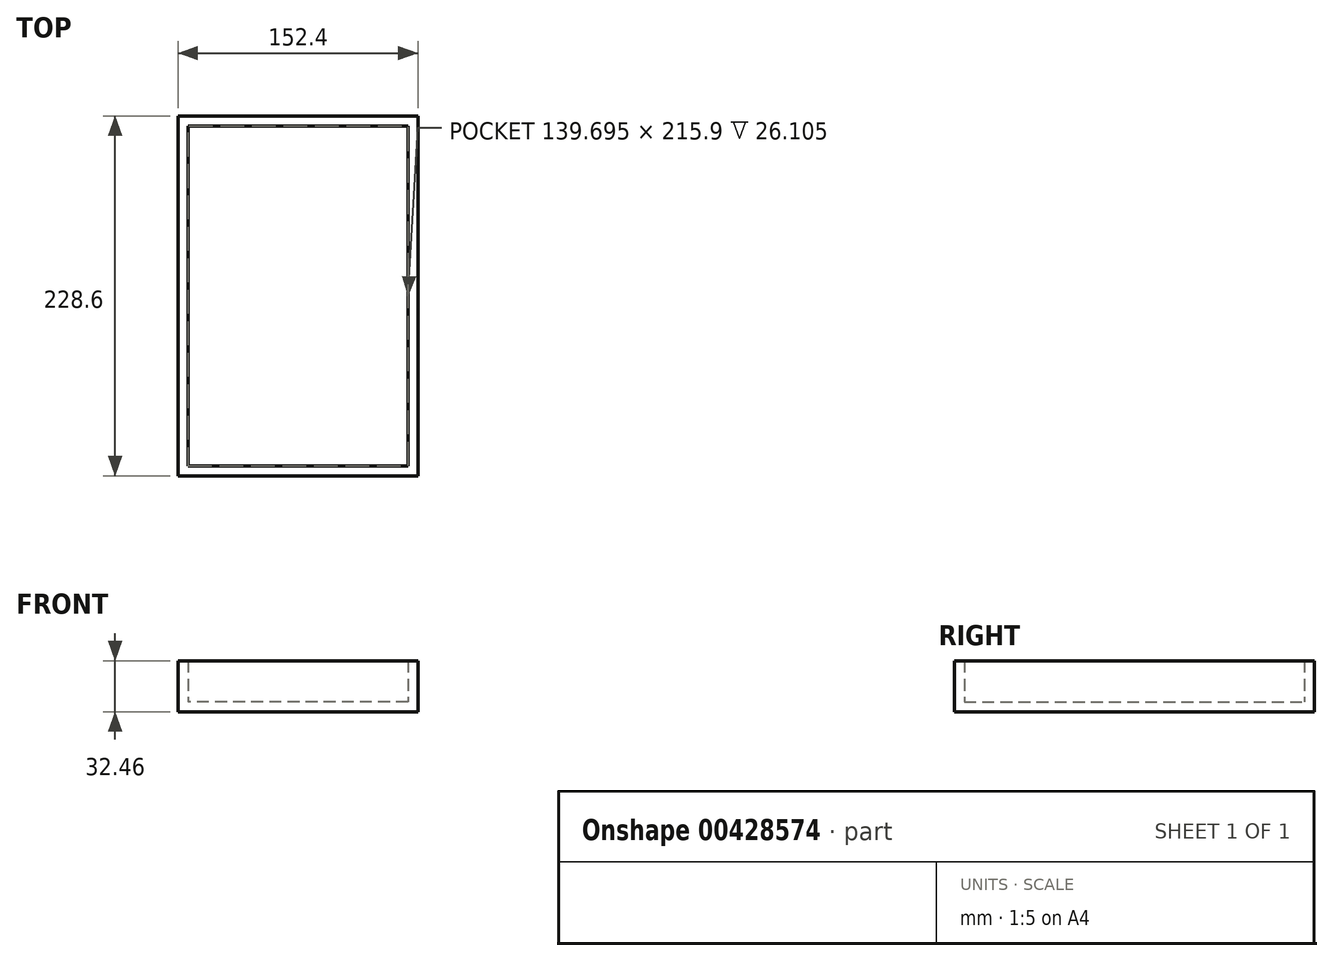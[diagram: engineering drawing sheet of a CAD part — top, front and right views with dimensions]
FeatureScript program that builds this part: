
annotation { "Feature Type Name" : "Feature", "Feature Type Description" : "" }
export const myFeature = defineFeature(function(context is Context, id is Id, definition is map)
    precondition{}
    {
        {
            var Q0;
            Q0=qCreatedBy(makeId("Front.planeOp"),FACE);
            var sketch = newSketch(context, id + "F0", { "sketchPlane" : qUnion([Q0])});
            skLineSegment(sketch, "E0.bottom", {"start": v(76.2, 16.23) * mm, "end": v(-76.2, 16.23) * mm});
            skLineSegment(sketch, "E0.top", {"start": v(76.2, -16.23) * mm, "end": v(-76.2, -16.23) * mm});
            skLineSegment(sketch, "E0.left", {"start": v(76.2, 16.23) * mm, "end": v(76.2, -16.23) * mm});
            skLineSegment(sketch, "E0.right", {"start": v(-76.2, 16.23) * mm, "end": v(-76.2, -16.23) * mm});
            skPoint(sketch, "E0.middle", {"position": v(0, 0) * mm});
            skSolve(sketch);
        }
        {
            var Q0;
            Q0=makeQuery(id+"F0.imprint","IMPRINT",FACE,{"disambiguationData":[TD([[makeQuery(id+"F0.imprint","IMPRINT",EDGE,{"derivedFrom":sQuery(id+"F0.wireOp",EDGE,"E0.bottom")}),1.0]])]});
            extrude(context, id + "F1", {"entities" : qUnion([Q0]), "depth" : 228.6 * mm});
        }
        {
            var Q0;
            Q0=makeQuery(id+"F1.opExtrude","SWEPT_FACE",FACE,{"disambiguationData":[OSD([sQuery(id+"F0.wireOp",EDGE,"E0.bottom")])]});
            shell(context, id + "F2", {"entities" : qUnion([Q0]), "thickness" : 6.35 * mm});
        }
    });
